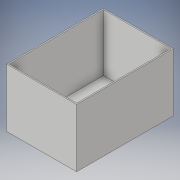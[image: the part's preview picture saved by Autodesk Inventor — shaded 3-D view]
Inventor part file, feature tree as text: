
AUTODESK INVENTOR PART (.ipt)
format: ipt  version: 2019 (Build 230136000, 136)  size: 99,328 bytes
history: native  units: mm
features: extrude x1, shell x1, sketch x1
ambient origin geometry x8: Origin, YZ Plane, XZ Plane, XY Plane, X Axis, Y Axis, Z Axis, Center Point
bodies: Solid1 (feature_tree)
feature tree (3):
  extrude  "Extrusion1"  Depth=830.0mm
  shell  "Shell1"  Thickness=500.0mm
  sketch  "Sketch1"  dims[d0=600.0mm d1=830.0mm d2=500.0mm d3=0.0mm d4=10.0mm]
